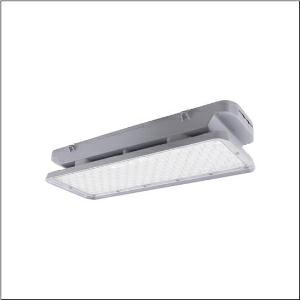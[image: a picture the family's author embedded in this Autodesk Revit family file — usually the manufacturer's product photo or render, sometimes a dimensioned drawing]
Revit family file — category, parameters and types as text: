
# Revit family: highbay_21-s_51hk42da4gca
name_source: partatom
category: Lighting Fixtures
units: mm (PartAtom-declared; Revit-internal decimal feet)

## family parameters
Cut with Voids When Loaded = No
Host = Face
Light Source = No
Part Type = Normal
Room Calculation Point = No
Round Connector Dimension = Use Diameter
Shared = No

## types (1)
- Highbay 21-S (1 x LED, 13500 lm, 75 W, 4000K)
    Apparent Load = 75 VA
    CIE Flux Codes = 74 96 100 100 100
    Color Rendering = 80
    Color Temperature = 4000K
    Default Elevation = 1800 mm
    Description = Highbay 21-S, LED high bay luminaire, primary light control with lens, of PC, light emission: direct distribution, primary light characteristic: symmetric, installation type: suspended mounting, surface-mounted, LED, rated luminous flux: 13.500lm, luminous efficacy: 179lm/W, light colour: 840, colour temperature: 4000K, with terminal, 5-pole, max. 2.5mm², mains connection: 220..240V, AC, 50Hz, rated input power: 75W, housing, of diecast aluminium, coated, grey, length: 471mm, width: 172mm, height: 87mm, protection rating (complete): IP66, insulation class (complete): insulation class I (protective earthing), certification: CE, ENEC, UKCA, protection symbol: D, impact resistance: IK08, permissible operating ambient temperature: -30..+60°C, corresponds to IFS (International Featured Standards) requirements for safety and quality in the food industry, LABS conformity tested according to VDMA 24364:2018-05, packaging unit: 1 piece
    Height = 89 mm
    Lamp = 1 x LED
    Lamp Light Flux = 13500 lm
    Lamp Power = 75 W
    Lamp count = 1
    Length = 471 mm
    Luminous efficacy = 180 lm/W
    Manufacturer = Siteco
    ModVariant = No
    Model = 51HK42DA4GCA
    Mounting Place = Ceiling
    Mounting Type = Pendant
    Number of Poles = 1
    OnlyDefault = Yes
    Power Factor = 1
    Product Name = Highbay 21-S
    Product group = LED high bay luminaire
    ProductGroupID = 903
    Protection Class = Protection class I
    Protection Degree = IP 66
    RLX_Detail_Level = 1
    RLX_Emergency_Light_Flux = 0 lm
    RLX_Emergency_Type = 0
    RLX_Emergency_Type_DB = No
    RlxData = <blob elided: 21961 chars, md5=98aa54c4>
    Socket = socket
    Standby Power = 0 W
    System Light Flux = 13500 lm
    System Power = 75 W
    Type Comments = Product without accessories
    Type Image = l_1276526.jpg
    URL = http://relux.com
    VarID = ---
    Voltage = 0 V
    Weight = 0.00 kg
    Width = 172 mm

## geometry (parser evidence)
native form markers: Blend x4, Sweep x13
no freeform markers — native parametric forms only
